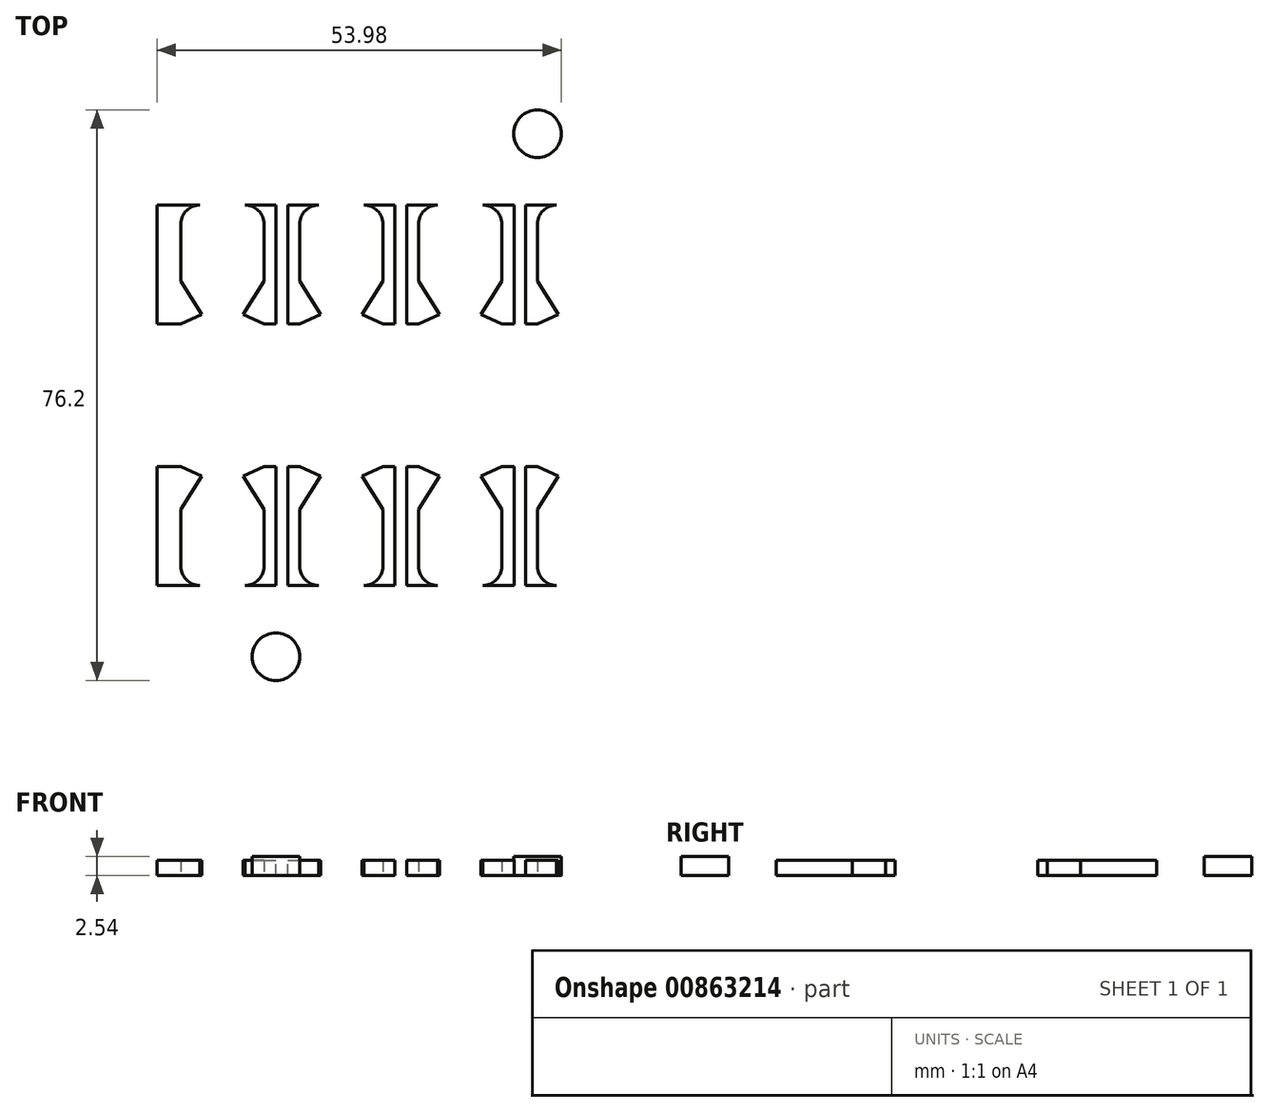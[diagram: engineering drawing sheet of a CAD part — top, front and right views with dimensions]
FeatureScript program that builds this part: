
annotation { "Feature Type Name" : "Feature", "Feature Type Description" : "" }
export const myFeature = defineFeature(function(context is Context, id is Id, definition is map)
    precondition{}
    {
        {
            var Q0;
            Q0=qCreatedBy(makeId("Top.planeOp"),FACE);
            var sketch = newSketch(context, id + "F0", { "sketchPlane" : qUnion([Q0])});
            skCircle(sketch, "E0", {"center": v(0, 0) * mm, "radius": 52.39 * mm});
            skLineSegment(sketch, "E1", {"start": v(-44.9, 26.99) * mm, "end": v(44.9, 26.99) * mm, "construction": true});
            skLineSegment(sketch, "E2", {"start": v(-44.9, -26.99) * mm, "end": v(44.9, -26.99) * mm, "construction": true});
            skLineSegment(sketch, "E3", {"start": v(-39.69, 26.99) * mm, "end": v(-39.69, -26.99) * mm, "construction": true});
            skLineSegment(sketch, "E4", {"start": v(39.69, 26.99) * mm, "end": v(39.69, -26.99) * mm, "construction": true});
            skLineSegment(sketch, "E5", {"start": v(28.57, 26.99) * mm, "end": v(28.58, -26.99) * mm, "construction": true});
            skLineSegment(sketch, "E6", {"start": v(-30.16, 26.99) * mm, "end": v(-30.16, -26.99) * mm, "construction": true});
            skLineSegment(sketch, "E7", {"start": v(-19.05, 26.99) * mm, "end": v(-19.05, -26.99) * mm, "construction": true});
            skLineSegment(sketch, "E8", {"start": v(-14.29, 26.99) * mm, "end": v(-14.29, -26.99) * mm, "construction": true});
            skLineSegment(sketch, "E9", {"start": v(-3.18, 26.99) * mm, "end": v(-3.17, -26.99) * mm, "construction": true});
            skLineSegment(sketch, "E10", {"start": v(1.59, 26.99) * mm, "end": v(1.59, -26.99) * mm, "construction": true});
            skLineSegment(sketch, "E11", {"start": v(12.7, 26.99) * mm, "end": v(12.7, -26.99) * mm, "construction": true});
            skLineSegment(sketch, "E12", {"start": v(17.46, 26.99) * mm, "end": v(17.46, -26.99) * mm, "construction": true});
            skLineSegment(sketch, "E13", {"start": v(-39.69, 25.4) * mm, "end": v(39.69, 25.4) * mm, "construction": true});
            skLineSegment(sketch, "E14", {"start": v(-39.69, -25.4) * mm, "end": v(39.69, -25.4) * mm, "construction": true});
            skLineSegment(sketch, "E15", {"start": v(-30.16, 9.53) * mm, "end": v(-27.37, 10.8) * mm});
            skLineSegment(sketch, "E16", {"start": v(-27.37, 10.8) * mm, "end": v(-30.16, 15.24) * mm});
            skLineSegment(sketch, "E17", {"start": v(-30.16, 15.24) * mm, "end": v(-30.16, 25.4) * mm});
            skLineSegment(sketch, "E18", {"start": v(-30.16, 25.4) * mm, "end": v(-33.34, 25.4) * mm});
            skLineSegment(sketch, "E19", {"start": v(-33.34, 25.4) * mm, "end": v(-33.34, 9.52) * mm});
            skLineSegment(sketch, "E20", {"start": v(-33.34, 9.52) * mm, "end": v(-30.16, 9.52) * mm});
            skLineSegment(sketch, "E21", {"start": v(-30.16, -25.4) * mm, "end": v(-30.16, -15.24) * mm});
            skLineSegment(sketch, "E22", {"start": v(-30.16, -15.24) * mm, "end": v(-27.37, -10.8) * mm});
            skLineSegment(sketch, "E23", {"start": v(-27.37, -10.8) * mm, "end": v(-30.16, -9.52) * mm});
            skLineSegment(sketch, "E24", {"start": v(-30.16, -9.53) * mm, "end": v(-33.34, -9.53) * mm});
            skLineSegment(sketch, "E25", {"start": v(-33.34, -9.53) * mm, "end": v(-33.34, -25.4) * mm});
            skLineSegment(sketch, "E26", {"start": v(-33.34, -25.4) * mm, "end": v(-30.16, -25.4) * mm});
            skLineSegment(sketch, "E27.1.0.1", {"start": v(-14.29, -9.53) * mm, "end": v(-17.46, -9.53) * mm});
            skLineSegment(sketch, "E27.1.0.2", {"start": v(-11.5, -10.8) * mm, "end": v(-14.29, -9.53) * mm});
            skLineSegment(sketch, "E27.1.0.3", {"start": v(-14.29, -15.24) * mm, "end": v(-11.5, -10.8) * mm});
            skLineSegment(sketch, "E27.1.0.4", {"start": v(-14.29, -25.4) * mm, "end": v(-14.29, -15.24) * mm});
            skLineSegment(sketch, "E27.2.0.1", {"start": v(1.59, -9.53) * mm, "end": v(-1.59, -9.53) * mm});
            skLineSegment(sketch, "E27.2.0.2", {"start": v(4.38, -10.8) * mm, "end": v(1.59, -9.53) * mm});
            skLineSegment(sketch, "E27.2.0.3", {"start": v(1.59, -15.24) * mm, "end": v(4.38, -10.8) * mm});
            skLineSegment(sketch, "E27.2.0.4", {"start": v(1.59, -25.4) * mm, "end": v(1.59, -15.24) * mm});
            skLineSegment(sketch, "E27.3.0.1", {"start": v(17.46, -9.53) * mm, "end": v(14.29, -9.53) * mm});
            skLineSegment(sketch, "E27.3.0.2", {"start": v(20.26, -10.8) * mm, "end": v(17.46, -9.53) * mm});
            skLineSegment(sketch, "E27.3.0.3", {"start": v(17.46, -15.24) * mm, "end": v(20.26, -10.8) * mm});
            skLineSegment(sketch, "E27.3.0.4", {"start": v(17.46, -25.4) * mm, "end": v(17.46, -15.24) * mm});
            skLineSegment(sketch, "E27.direction1", {"start": v(-33.34, -25.4) * mm, "end": v(-17.59, -25.4) * mm, "construction": true});
            skLineSegment(sketch, "E28", {"start": v(-34.92, 25.4) * mm, "end": v(-34.92, -25.4) * mm});
            skLineSegment(sketch, "E29", {"start": v(-34.92, -25.4) * mm, "end": v(-33.34, -25.4) * mm});
            skLineSegment(sketch, "E30", {"start": v(-30.16, -25.4) * mm, "end": v(-17.59, -25.4) * mm});
            skLineSegment(sketch, "E31", {"start": v(-14.29, -25.4) * mm, "end": v(-1.71, -25.4) * mm});
            skLineSegment(sketch, "E32", {"start": v(1.59, -25.4) * mm, "end": v(14.16, -25.4) * mm});
            skLineSegment(sketch, "E33", {"start": v(17.46, -25.4) * mm, "end": v(28.58, -25.4) * mm});
            skLineSegment(sketch, "E34", {"start": v(28.58, -25.4) * mm, "end": v(28.57, 25.4) * mm});
            skLineSegment(sketch, "E35.1.0.1", {"start": v(-17.46, 9.52) * mm, "end": v(-14.29, 9.52) * mm});
            skLineSegment(sketch, "E35.1.0.2", {"start": v(-14.29, 9.52) * mm, "end": v(-11.5, 10.8) * mm});
            skLineSegment(sketch, "E35.1.0.3", {"start": v(-11.5, 10.8) * mm, "end": v(-14.29, 15.24) * mm});
            skLineSegment(sketch, "E35.1.0.4", {"start": v(-14.29, 15.24) * mm, "end": v(-14.29, 25.4) * mm});
            skLineSegment(sketch, "E35.2.0.1", {"start": v(-1.59, 9.52) * mm, "end": v(1.59, 9.52) * mm});
            skLineSegment(sketch, "E35.2.0.2", {"start": v(1.59, 9.53) * mm, "end": v(4.38, 10.8) * mm});
            skLineSegment(sketch, "E35.2.0.3", {"start": v(4.38, 10.8) * mm, "end": v(1.59, 15.24) * mm});
            skLineSegment(sketch, "E35.2.0.4", {"start": v(1.59, 15.24) * mm, "end": v(1.59, 25.4) * mm});
            skLineSegment(sketch, "E35.3.0.1", {"start": v(14.29, 9.52) * mm, "end": v(17.46, 9.52) * mm});
            skLineSegment(sketch, "E35.3.0.2", {"start": v(17.46, 9.53) * mm, "end": v(20.26, 10.8) * mm});
            skLineSegment(sketch, "E35.3.0.3", {"start": v(20.26, 10.8) * mm, "end": v(17.46, 15.24) * mm});
            skLineSegment(sketch, "E35.3.0.4", {"start": v(17.46, 15.24) * mm, "end": v(17.46, 25.4) * mm});
            skLineSegment(sketch, "E35.direction1", {"start": v(-33.34, 9.53) * mm, "end": v(-17.46, 9.53) * mm, "construction": true});
            skLineSegment(sketch, "E36", {"start": v(28.57, 25.4) * mm, "end": v(17.46, 25.4) * mm});
            skLineSegment(sketch, "E37", {"start": v(14.29, 25.4) * mm, "end": v(1.59, 25.4) * mm});
            skLineSegment(sketch, "E38", {"start": v(-1.59, 25.4) * mm, "end": v(-14.29, 25.4) * mm});
            skLineSegment(sketch, "E39", {"start": v(-17.46, 25.4) * mm, "end": v(-30.16, 25.4) * mm});
            skLineSegment(sketch, "E40", {"start": v(-34.92, 25.4) * mm, "end": v(-33.34, 25.4) * mm});
            skLineSegment(sketch, "E41", {"start": v(-19.05, 9.52) * mm, "end": v(-14.29, 9.52) * mm});
            skLineSegment(sketch, "E42", {"start": v(-16.67, 9.52) * mm, "end": v(-16.67, 25.4) * mm, "construction": true});
            skLineSegment(sketch, "E43", {"start": v(-3.18, 9.52) * mm, "end": v(1.59, 9.52) * mm});
            skLineSegment(sketch, "E44", {"start": v(-0.8, 9.52) * mm, "end": v(-0.8, 25.4) * mm, "construction": true});
            skLineSegment(sketch, "E45", {"start": v(12.7, 9.52) * mm, "end": v(17.46, 9.52) * mm});
            skLineSegment(sketch, "E46", {"start": v(15.08, 9.52) * mm, "end": v(15.08, 25.4) * mm, "construction": true});
            skLineSegment(sketch, "E47.MirrorCS", {"start": v(-21.84, 10.8) * mm, "end": v(-19.05, 15.24) * mm});
            skLineSegment(sketch, "E48.MirrorCS", {"start": v(-19.05, 9.52) * mm, "end": v(-21.84, 10.8) * mm});
            skLineSegment(sketch, "E49.MirrorCS", {"start": v(-5.97, 10.8) * mm, "end": v(-3.17, 15.24) * mm});
            skLineSegment(sketch, "E50.MirrorCS", {"start": v(-3.17, 9.53) * mm, "end": v(-5.97, 10.8) * mm});
            skLineSegment(sketch, "E51.MirrorCS", {"start": v(9.9, 10.8) * mm, "end": v(12.7, 15.24) * mm});
            skLineSegment(sketch, "E52.MirrorCS", {"start": v(12.7, 9.53) * mm, "end": v(9.9, 10.8) * mm});
            skLineSegment(sketch, "E53", {"start": v(-14.29, -9.53) * mm, "end": v(-19.05, -9.53) * mm});
            skLineSegment(sketch, "E54", {"start": v(-16.67, -9.53) * mm, "end": v(-16.67, -25.4) * mm, "construction": true});
            skLineSegment(sketch, "E55", {"start": v(-3.17, -9.53) * mm, "end": v(1.59, -9.53) * mm});
            skLineSegment(sketch, "E56", {"start": v(-0.8, -9.53) * mm, "end": v(-0.8, -25.4) * mm, "construction": true});
            skLineSegment(sketch, "E57", {"start": v(12.7, -9.53) * mm, "end": v(17.46, -9.53) * mm});
            skLineSegment(sketch, "E58", {"start": v(15.08, -9.53) * mm, "end": v(15.08, -25.4) * mm, "construction": true});
            skLineSegment(sketch, "E59.MirrorCS", {"start": v(-19.05, 15.24) * mm, "end": v(-19.05, 25.4) * mm});
            skLineSegment(sketch, "E60.MirrorCS", {"start": v(-32.54, 9.52) * mm, "end": v(-32.54, 25.4) * mm, "construction": true});
            skLineSegment(sketch, "E61.MirrorCS", {"start": v(-3.17, 15.24) * mm, "end": v(-3.17, 25.4) * mm});
            skLineSegment(sketch, "E62.MirrorCS", {"start": v(12.7, 15.24) * mm, "end": v(12.7, 25.4) * mm});
            skLineSegment(sketch, "E63.MirrorCS", {"start": v(-19.05, -25.4) * mm, "end": v(-19.05, -15.24) * mm});
            skLineSegment(sketch, "E64.MirrorCS", {"start": v(-19.05, -15.24) * mm, "end": v(-21.84, -10.8) * mm});
            skLineSegment(sketch, "E65.MirrorCS", {"start": v(-21.84, -10.8) * mm, "end": v(-19.05, -9.53) * mm});
            skLineSegment(sketch, "E66.MirrorCS", {"start": v(-3.17, -25.4) * mm, "end": v(-3.17, -15.24) * mm});
            skLineSegment(sketch, "E67.MirrorCS", {"start": v(-3.17, -15.24) * mm, "end": v(-5.97, -10.8) * mm});
            skLineSegment(sketch, "E68.MirrorCS", {"start": v(-5.97, -10.8) * mm, "end": v(-3.17, -9.53) * mm});
            skLineSegment(sketch, "E69.MirrorCS", {"start": v(12.7, -25.4) * mm, "end": v(12.7, -15.24) * mm});
            skLineSegment(sketch, "E70.MirrorCS", {"start": v(12.7, -15.24) * mm, "end": v(9.9, -10.8) * mm});
            skLineSegment(sketch, "E71.MirrorCS", {"start": v(9.9, -10.8) * mm, "end": v(12.7, -9.53) * mm});
            skSolve(sketch);
        }
        {
            var Q0;
            Q0=makeQuery(id+"F0.imprint","IMPRINT",FACE,{"disambiguationData":[TD([[makeQuery(id+"F0.imprint","IMPRINT",EDGE,{"derivedFrom":sQuery(id+"F0.wireOp",EDGE,"E0")}),1.0]])]});
            var Q1;
            Q1=makeQuery(id+"F0.imprint","IMPRINT",FACE,{"disambiguationData":[TD([[makeQuery(id+"F0.imprint","IMPRINT",EDGE,{"derivedFrom":sQuery(id+"F0.wireOp",EDGE,"E15")}),1.0]])]});
            var Q2;
            Q2=makeQuery(id+"F0.imprint","IMPRINT",FACE,{"disambiguationData":[TD([[makeQuery(id+"F0.imprint","IMPRINT",EDGE,{"derivedFrom":sQuery(id+"F0.wireOp",EDGE,"E21")}),1.0]])]});
            extrude(context, id + "F1", {"entities" : qUnion([Q0, Q1, Q2]), "depth" : 2.54 * mm, "offsetDistance" : 25.4 * mm});
        }
        {
            var Q0;
            Q0=makeQuery(id+"F1.opExtrude","SWEPT_EDGE",EDGE,{"disambiguationData":[OSD([sQuery(id+"F0.wireOp",EDGE,"E17"),sQuery(id+"F0.wireOp",EDGE,"E18"),sQuery(id+"F0.wireOp",EDGE,"E39")])]});
            var Q1;
            Q1=makeQuery(id+"F1.opExtrude","SWEPT_EDGE",EDGE,{"disambiguationData":[OSD([sQuery(id+"F0.wireOp",EDGE,"E35.1.0.4"),sQuery(id+"F0.wireOp",EDGE,"E38")])]});
            var Q2;
            Q2=makeQuery(id+"F1.opExtrude","SWEPT_EDGE",EDGE,{"disambiguationData":[OSD([sQuery(id+"F0.wireOp",EDGE,"E35.2.0.4"),sQuery(id+"F0.wireOp",EDGE,"E37")])]});
            var Q3;
            Q3=makeQuery(id+"F1.opExtrude","SWEPT_EDGE",EDGE,{"disambiguationData":[OSD([sQuery(id+"F0.wireOp",EDGE,"E35.3.0.4"),sQuery(id+"F0.wireOp",EDGE,"E36")])]});
            var Q4;
            Q4=makeQuery(id+"F1.opExtrude","SWEPT_EDGE",EDGE,{"disambiguationData":[OSD([sQuery(id+"F0.wireOp",EDGE,"E27.3.0.4"),sQuery(id+"F0.wireOp",EDGE,"E33")])]});
            var Q5;
            Q5=makeQuery(id+"F1.opExtrude","SWEPT_EDGE",EDGE,{"disambiguationData":[OSD([sQuery(id+"F0.wireOp",EDGE,"E27.2.0.4"),sQuery(id+"F0.wireOp",EDGE,"E32")])]});
            var Q6;
            Q6=makeQuery(id+"F1.opExtrude","SWEPT_EDGE",EDGE,{"disambiguationData":[OSD([sQuery(id+"F0.wireOp",EDGE,"E27.1.0.4"),sQuery(id+"F0.wireOp",EDGE,"E31")])]});
            var Q7;
            Q7=makeQuery(id+"F1.opExtrude","SWEPT_EDGE",EDGE,{"disambiguationData":[OSD([sQuery(id+"F0.wireOp",EDGE,"E21"),sQuery(id+"F0.wireOp",EDGE,"E26"),sQuery(id+"F0.wireOp",EDGE,"E30")])]});
            var Q8;
            Q8=makeQuery(id+"F1.opExtrude","SWEPT_EDGE",EDGE,{"disambiguationData":[OSD([sQuery(id+"F0.wireOp",EDGE,"E30"),sQuery(id+"F0.wireOp",EDGE,"E63.MirrorCS")])]});
            var Q9;
            Q9=makeQuery(id+"F1.opExtrude","SWEPT_EDGE",EDGE,{"disambiguationData":[OSD([sQuery(id+"F0.wireOp",EDGE,"E31"),sQuery(id+"F0.wireOp",EDGE,"E66.MirrorCS")])]});
            var Q10;
            Q10=makeQuery(id+"F1.opExtrude","SWEPT_EDGE",EDGE,{"disambiguationData":[OSD([sQuery(id+"F0.wireOp",EDGE,"E32"),sQuery(id+"F0.wireOp",EDGE,"E69.MirrorCS")])]});
            var Q11;
            Q11=makeQuery(id+"F1.opExtrude","SWEPT_EDGE",EDGE,{"disambiguationData":[OSD([sQuery(id+"F0.wireOp",EDGE,"E37"),sQuery(id+"F0.wireOp",EDGE,"E62.MirrorCS")])]});
            var Q12;
            Q12=makeQuery(id+"F1.opExtrude","SWEPT_EDGE",EDGE,{"disambiguationData":[OSD([sQuery(id+"F0.wireOp",EDGE,"E38"),sQuery(id+"F0.wireOp",EDGE,"E61.MirrorCS")])]});
            var Q13;
            Q13=makeQuery(id+"F1.opExtrude","SWEPT_EDGE",EDGE,{"disambiguationData":[OSD([sQuery(id+"F0.wireOp",EDGE,"E39"),sQuery(id+"F0.wireOp",EDGE,"E59.MirrorCS")])]});
            fillet(context, id + "F2", {"entities" : qUnion([Q0, Q1, Q2, Q3, Q4, Q5, Q6, Q7, Q8, Q9, Q10, Q11, Q12, Q13]), "radius" : 2.54 * mm, "tangentPropagation" : true, "allowEdgeOverflow" : false});
        }
        {
            var Q0;
            Q0=makeQuery(id+"F1.opExtrude","CAP_FACE",FACE,{"disambiguationData":[OSD([sQuery(id+"F0.wireOp",EDGE,"E0"),sQuery(id+"F0.wireOp",EDGE,"E15"),sQuery(id+"F0.wireOp",EDGE,"E16"),sQuery(id+"F0.wireOp",EDGE,"E17"),sQuery(id+"F0.wireOp",EDGE,"E19"),sQuery(id+"F0.wireOp",EDGE,"E20"),sQuery(id+"F0.wireOp",EDGE,"E21"),sQuery(id+"F0.wireOp",EDGE,"E22"),sQuery(id+"F0.wireOp",EDGE,"E23"),sQuery(id+"F0.wireOp",EDGE,"E24"),sQuery(id+"F0.wireOp",EDGE,"E25"),sQuery(id+"F0.wireOp",EDGE,"E27.1.0.0"),sQuery(id+"F0.wireOp",EDGE,"E27.1.0.1"),sQuery(id+"F0.wireOp",EDGE,"E27.1.0.2"),sQuery(id+"F0.wireOp",EDGE,"E27.1.0.3"),sQuery(id+"F0.wireOp",EDGE,"E27.1.0.4"),sQuery(id+"F0.wireOp",EDGE,"E27.2.0.0"),sQuery(id+"F0.wireOp",EDGE,"E27.2.0.1"),sQuery(id+"F0.wireOp",EDGE,"E27.2.0.2"),sQuery(id+"F0.wireOp",EDGE,"E27.2.0.3"),sQuery(id+"F0.wireOp",EDGE,"E27.2.0.4"),sQuery(id+"F0.wireOp",EDGE,"E27.3.0.0"),sQuery(id+"F0.wireOp",EDGE,"E27.3.0.1"),sQuery(id+"F0.wireOp",EDGE,"E27.3.0.2"),sQuery(id+"F0.wireOp",EDGE,"E27.3.0.3"),sQuery(id+"F0.wireOp",EDGE,"E27.3.0.4"),sQuery(id+"F0.wireOp",EDGE,"E28"),sQuery(id+"F0.wireOp",EDGE,"E29"),sQuery(id+"F0.wireOp",EDGE,"E30"),sQuery(id+"F0.wireOp",EDGE,"E31"),sQuery(id+"F0.wireOp",EDGE,"E32"),sQuery(id+"F0.wireOp",EDGE,"E33"),sQuery(id+"F0.wireOp",EDGE,"E34"),sQuery(id+"F0.wireOp",EDGE,"E35.1.0.0"),sQuery(id+"F0.wireOp",EDGE,"E35.1.0.1"),sQuery(id+"F0.wireOp",EDGE,"E35.1.0.2"),sQuery(id+"F0.wireOp",EDGE,"E35.1.0.3"),sQuery(id+"F0.wireOp",EDGE,"E35.1.0.4"),sQuery(id+"F0.wireOp",EDGE,"E35.2.0.0"),sQuery(id+"F0.wireOp",EDGE,"E35.2.0.1"),sQuery(id+"F0.wireOp",EDGE,"E35.2.0.2"),sQuery(id+"F0.wireOp",EDGE,"E35.2.0.3"),sQuery(id+"F0.wireOp",EDGE,"E35.2.0.4"),sQuery(id+"F0.wireOp",EDGE,"E35.3.0.0"),sQuery(id+"F0.wireOp",EDGE,"E35.3.0.1"),sQuery(id+"F0.wireOp",EDGE,"E35.3.0.2"),sQuery(id+"F0.wireOp",EDGE,"E35.3.0.3"),sQuery(id+"F0.wireOp",EDGE,"E35.3.0.4"),sQuery(id+"F0.wireOp",EDGE,"E36"),sQuery(id+"F0.wireOp",EDGE,"E37"),sQuery(id+"F0.wireOp",EDGE,"E38"),sQuery(id+"F0.wireOp",EDGE,"E39"),sQuery(id+"F0.wireOp",EDGE,"E40")])],"isStart":false});
            var sketch = newSketch(context, id + "F3", { "sketchPlane" : qUnion([Q0])});
            skLineSegment(sketch, "E72.bottom", {"start": v(-34.92, 25.4) * mm, "end": v(28.58, 25.4) * mm});
            skLineSegment(sketch, "E72.top", {"start": v(-34.92, -25.4) * mm, "end": v(28.58, -25.4) * mm});
            skLineSegment(sketch, "E72.left", {"start": v(-34.92, 25.4) * mm, "end": v(-34.92, -25.4) * mm});
            skLineSegment(sketch, "E72.right", {"start": v(28.58, 25.4) * mm, "end": v(28.58, -25.4) * mm});
            skSolve(sketch);
        }
        {
            var Q0;
            Q0 = qSketchRegion(id + "F3", true);
            extrude(context, id + "F4", {"entities" : qUnion([Q0]), "operationType" : NewBodyOperationType.REMOVE, "oppositeDirection" : true, "depth" : 0.5 * mm, "offsetDistance" : 25.4 * mm});
        }
        {
            var Q0;
            Q0=makeQuery(id+"F1.opExtrude","CAP_FACE",FACE,{"disambiguationData":[OSD([sQuery(id+"F0.wireOp",EDGE,"E0"),sQuery(id+"F0.wireOp",EDGE,"E15"),sQuery(id+"F0.wireOp",EDGE,"E16"),sQuery(id+"F0.wireOp",EDGE,"E17"),sQuery(id+"F0.wireOp",EDGE,"E19"),sQuery(id+"F0.wireOp",EDGE,"E20"),sQuery(id+"F0.wireOp",EDGE,"E21"),sQuery(id+"F0.wireOp",EDGE,"E22"),sQuery(id+"F0.wireOp",EDGE,"E23"),sQuery(id+"F0.wireOp",EDGE,"E24"),sQuery(id+"F0.wireOp",EDGE,"E25"),sQuery(id+"F0.wireOp",EDGE,"E27.1.0.0"),sQuery(id+"F0.wireOp",EDGE,"E27.1.0.1"),sQuery(id+"F0.wireOp",EDGE,"E27.1.0.2"),sQuery(id+"F0.wireOp",EDGE,"E27.1.0.3"),sQuery(id+"F0.wireOp",EDGE,"E27.1.0.4"),sQuery(id+"F0.wireOp",EDGE,"E27.2.0.0"),sQuery(id+"F0.wireOp",EDGE,"E27.2.0.1"),sQuery(id+"F0.wireOp",EDGE,"E27.2.0.2"),sQuery(id+"F0.wireOp",EDGE,"E27.2.0.3"),sQuery(id+"F0.wireOp",EDGE,"E27.2.0.4"),sQuery(id+"F0.wireOp",EDGE,"E27.3.0.0"),sQuery(id+"F0.wireOp",EDGE,"E27.3.0.1"),sQuery(id+"F0.wireOp",EDGE,"E27.3.0.2"),sQuery(id+"F0.wireOp",EDGE,"E27.3.0.3"),sQuery(id+"F0.wireOp",EDGE,"E27.3.0.4"),sQuery(id+"F0.wireOp",EDGE,"E28"),sQuery(id+"F0.wireOp",EDGE,"E29"),sQuery(id+"F0.wireOp",EDGE,"E30"),sQuery(id+"F0.wireOp",EDGE,"E31"),sQuery(id+"F0.wireOp",EDGE,"E32"),sQuery(id+"F0.wireOp",EDGE,"E33"),sQuery(id+"F0.wireOp",EDGE,"E34"),sQuery(id+"F0.wireOp",EDGE,"E35.1.0.0"),sQuery(id+"F0.wireOp",EDGE,"E35.1.0.1"),sQuery(id+"F0.wireOp",EDGE,"E35.1.0.2"),sQuery(id+"F0.wireOp",EDGE,"E35.1.0.3"),sQuery(id+"F0.wireOp",EDGE,"E35.1.0.4"),sQuery(id+"F0.wireOp",EDGE,"E35.2.0.0"),sQuery(id+"F0.wireOp",EDGE,"E35.2.0.1"),sQuery(id+"F0.wireOp",EDGE,"E35.2.0.2"),sQuery(id+"F0.wireOp",EDGE,"E35.2.0.3"),sQuery(id+"F0.wireOp",EDGE,"E35.2.0.4"),sQuery(id+"F0.wireOp",EDGE,"E35.3.0.0"),sQuery(id+"F0.wireOp",EDGE,"E35.3.0.1"),sQuery(id+"F0.wireOp",EDGE,"E35.3.0.2"),sQuery(id+"F0.wireOp",EDGE,"E35.3.0.3"),sQuery(id+"F0.wireOp",EDGE,"E35.3.0.4"),sQuery(id+"F0.wireOp",EDGE,"E36"),sQuery(id+"F0.wireOp",EDGE,"E37"),sQuery(id+"F0.wireOp",EDGE,"E38"),sQuery(id+"F0.wireOp",EDGE,"E39"),sQuery(id+"F0.wireOp",EDGE,"E40")])],"isStart":false});
            var sketch = newSketch(context, id + "F5", { "sketchPlane" : qUnion([Q0])});
            skCircle(sketch, "E73", {"center": v(0, 0) * mm, "radius": 47 * mm});
            skCircle(sketch, "E74", {"center": v(0, 0) * mm, "radius": 52.39 * mm});
            skLineSegment(sketch, "E75", {"start": v(-41.4, 22.22) * mm, "end": v(41.4, 22.23) * mm, "construction": true});
            skLineSegment(sketch, "E76", {"start": v(-41.4, -22.23) * mm, "end": v(41.4, -22.22) * mm, "construction": true});
            skLineSegment(sketch, "E77", {"start": v(38.9, 22.23) * mm, "end": v(38.9, -22.22) * mm, "construction": true});
            skLineSegment(sketch, "E78", {"start": v(-38.9, 22.22) * mm, "end": v(-38.9, -22.23) * mm, "construction": true});
            skCircle(sketch, "E79.1.0", {"center": v(-38.5, 22.23) * mm, "radius": 2.38 * mm});
            skCircle(sketch, "E79.2.0", {"center": v(-38.5, -22.22) * mm, "radius": 2.38 * mm});
            skCircle(sketch, "E79.4.0", {"center": v(38.5, -22.23) * mm, "radius": 2.38 * mm});
            skCircle(sketch, "E79.5.0", {"center": v(38.5, 22.23) * mm, "radius": 2.38 * mm});
            skCircle(sketch, "E80", {"center": v(17.46, -34.93) * mm, "radius": 3.18 * mm});
            skCircle(sketch, "E81.MirrorC", {"center": v(17.46, 34.93) * mm, "radius": 3.18 * mm});
            skCircle(sketch, "E82.MirrorC", {"center": v(-17.46, 34.93) * mm, "radius": 3.18 * mm});
            skCircle(sketch, "E83.MirrorC", {"center": v(-17.46, -34.93) * mm, "radius": 3.18 * mm});
            skSolve(sketch);
        }
        {
            var Q0;
            Q0=makeQuery(id+"F5.imprint","IMPRINT",FACE,{"disambiguationData":[TD([[makeQuery(id+"F5.imprint","IMPRINT",EDGE,{"derivedFrom":sQuery(id+"F5.wireOp",EDGE,"E74")}),1.0]])]});
            var Q1;
            {var subQ0=sQuery(id+"F5.wireOp",EDGE,"E79.1.0");var subQ1=sQuery(id+"F5.wireOp",EDGE,"E73");var subQ2=makeQuery(id+"F5.imprint","INTERSECT",VERTEX,{"disambiguationData":[OD(0.0)],"derivedFrom":[subQ1,subQ0]});Q1=makeQuery(id+"F5.imprint","IMPRINT",FACE,{"disambiguationData":[TD([[makeQuery(id+"F5.imprint","IMPRINT",EDGE,{"disambiguationData":[TD([[subQ2,-1.0]])],"derivedFrom":subQ1}),-1.0]])]});}
            var Q2;
            {var subQ0=sQuery(id+"F5.wireOp",EDGE,"E79.2.0");var subQ1=sQuery(id+"F5.wireOp",EDGE,"E73");var subQ2=makeQuery(id+"F5.imprint","INTERSECT",VERTEX,{"disambiguationData":[OD(0.0)],"derivedFrom":[subQ1,subQ0]});Q2=makeQuery(id+"F5.imprint","IMPRINT",FACE,{"disambiguationData":[TD([[makeQuery(id+"F5.imprint","IMPRINT",EDGE,{"disambiguationData":[TD([[subQ2,-1.0]])],"derivedFrom":subQ1}),-1.0]])]});}
            var Q3;
            {var subQ0=sQuery(id+"F5.wireOp",EDGE,"E79.5.0");var subQ1=sQuery(id+"F5.wireOp",EDGE,"E73");var subQ2=makeQuery(id+"F5.imprint","INTERSECT",VERTEX,{"disambiguationData":[OD(0.0)],"derivedFrom":[subQ1,subQ0]});Q3=makeQuery(id+"F5.imprint","IMPRINT",FACE,{"disambiguationData":[TD([[makeQuery(id+"F5.imprint","IMPRINT",EDGE,{"disambiguationData":[TD([[subQ2,1.0]])],"derivedFrom":subQ1}),-1.0]])]});}
            var Q4;
            {var subQ0=sQuery(id+"F5.wireOp",EDGE,"E79.4.0");var subQ1=sQuery(id+"F5.wireOp",EDGE,"E73");var subQ2=makeQuery(id+"F5.imprint","INTERSECT",VERTEX,{"disambiguationData":[OD(0.0)],"derivedFrom":[subQ1,subQ0]});Q4=makeQuery(id+"F5.imprint","IMPRINT",FACE,{"disambiguationData":[TD([[makeQuery(id+"F5.imprint","IMPRINT",EDGE,{"disambiguationData":[TD([[subQ2,-1.0]])],"derivedFrom":subQ1}),-1.0]])]});}
            var Q5;
            Q5=makeQuery(id+"F5.imprint","IMPRINT",FACE,{"disambiguationData":[TD([[makeQuery(id+"F5.imprint","IMPRINT",EDGE,{"derivedFrom":sQuery(id+"F5.wireOp",EDGE,"E79.5.0")}),1.0]])]});
            var Q6;
            {var subQ0=sQuery(id+"F5.wireOp",EDGE,"E79.1.0");var subQ1=makeQuery(id+"F1.opExtrude","CAP_EDGE",EDGE,{"disambiguationData":[OSD([sQuery(id+"F0.wireOp",EDGE,"E28")])],"isStart":false});var subQ2=makeQuery(id+"F5.imprint","INTERSECT",VERTEX,{"disambiguationData":[OD(0.0)],"derivedFrom":[subQ1,subQ0]});Q6=makeQuery(id+"F5.imprint","IMPRINT",FACE,{"disambiguationData":[TD([[makeQuery(id+"F5.imprint","IMPRINT",EDGE,{"disambiguationData":[TD([[subQ2,-1.0]])],"derivedFrom":subQ0}),1.0]])]});}
            var Q7;
            {var subQ0=sQuery(id+"F5.wireOp",EDGE,"E79.2.0");var subQ1=makeQuery(id+"F1.opExtrude","CAP_EDGE",EDGE,{"disambiguationData":[OSD([sQuery(id+"F0.wireOp",EDGE,"E28")])],"isStart":false});var subQ2=makeQuery(id+"F5.imprint","INTERSECT",VERTEX,{"disambiguationData":[OD(0.0)],"derivedFrom":[subQ1,subQ0]});Q7=makeQuery(id+"F5.imprint","IMPRINT",FACE,{"disambiguationData":[TD([[makeQuery(id+"F5.imprint","IMPRINT",EDGE,{"disambiguationData":[TD([[subQ2,1.0]])],"derivedFrom":subQ0}),1.0]])]});}
            var Q8;
            Q8=makeQuery(id+"F5.imprint","IMPRINT",FACE,{"disambiguationData":[TD([[makeQuery(id+"F5.imprint","IMPRINT",EDGE,{"derivedFrom":sQuery(id+"F5.wireOp",EDGE,"E79.4.0")}),1.0]])]});
            var Q9;
            Q9=makeQuery(id+"F5.imprint","IMPRINT",FACE,{"disambiguationData":[TD([[makeQuery(id+"F5.imprint","IMPRINT",EDGE,{"derivedFrom":sQuery(id+"F5.wireOp",EDGE,"E80")}),1.0]])]});
            var Q10;
            Q10=makeQuery(id+"F5.imprint","IMPRINT",FACE,{"disambiguationData":[TD([[makeQuery(id+"F5.imprint","IMPRINT",EDGE,{"derivedFrom":sQuery(id+"F5.wireOp",EDGE,"E81.MirrorC")}),-1.0]])]});
            var Q11;
            Q11=makeQuery(id+"F5.imprint","IMPRINT",FACE,{"disambiguationData":[TD([[makeQuery(id+"F5.imprint","IMPRINT",EDGE,{"derivedFrom":sQuery(id+"F5.wireOp",EDGE,"E82.MirrorC")}),1.0]])]});
            var Q12;
            Q12=makeQuery(id+"F5.imprint","IMPRINT",FACE,{"disambiguationData":[TD([[makeQuery(id+"F5.imprint","IMPRINT",EDGE,{"derivedFrom":sQuery(id+"F5.wireOp",EDGE,"E83.MirrorC")}),-1.0]])]});
            extrude(context, id + "F6", {"entities" : qUnion([Q0, Q1, Q2, Q3, Q4, Q5, Q6, Q7, Q8, Q9, Q10, Q11, Q12]), "operationType" : NewBodyOperationType.REMOVE, "oppositeDirection" : true, "depth" : 25.4 * mm, "offsetDistance" : 25.4 * mm});
        }
        {
            var Q0;
            Q0=makeQuery(id+"F1.opExtrude","CAP_FACE",FACE,{"disambiguationData":[OSD([sQuery(id+"F0.wireOp",EDGE,"E0"),sQuery(id+"F0.wireOp",EDGE,"E15"),sQuery(id+"F0.wireOp",EDGE,"E16"),sQuery(id+"F0.wireOp",EDGE,"E17"),sQuery(id+"F0.wireOp",EDGE,"E19"),sQuery(id+"F0.wireOp",EDGE,"E20"),sQuery(id+"F0.wireOp",EDGE,"E21"),sQuery(id+"F0.wireOp",EDGE,"E22"),sQuery(id+"F0.wireOp",EDGE,"E23"),sQuery(id+"F0.wireOp",EDGE,"E24"),sQuery(id+"F0.wireOp",EDGE,"E25"),sQuery(id+"F0.wireOp",EDGE,"E27.1.0.2"),sQuery(id+"F0.wireOp",EDGE,"E27.1.0.3"),sQuery(id+"F0.wireOp",EDGE,"E27.1.0.4"),sQuery(id+"F0.wireOp",EDGE,"E27.2.0.2"),sQuery(id+"F0.wireOp",EDGE,"E27.2.0.3"),sQuery(id+"F0.wireOp",EDGE,"E27.2.0.4"),sQuery(id+"F0.wireOp",EDGE,"E27.3.0.2"),sQuery(id+"F0.wireOp",EDGE,"E27.3.0.3"),sQuery(id+"F0.wireOp",EDGE,"E27.3.0.4"),sQuery(id+"F0.wireOp",EDGE,"E28"),sQuery(id+"F0.wireOp",EDGE,"E29"),sQuery(id+"F0.wireOp",EDGE,"E30"),sQuery(id+"F0.wireOp",EDGE,"E31"),sQuery(id+"F0.wireOp",EDGE,"E32"),sQuery(id+"F0.wireOp",EDGE,"E33"),sQuery(id+"F0.wireOp",EDGE,"E34"),sQuery(id+"F0.wireOp",EDGE,"E35.1.0.2"),sQuery(id+"F0.wireOp",EDGE,"E35.1.0.3"),sQuery(id+"F0.wireOp",EDGE,"E35.1.0.4"),sQuery(id+"F0.wireOp",EDGE,"E35.2.0.2"),sQuery(id+"F0.wireOp",EDGE,"E35.2.0.3"),sQuery(id+"F0.wireOp",EDGE,"E35.2.0.4"),sQuery(id+"F0.wireOp",EDGE,"E35.3.0.2"),sQuery(id+"F0.wireOp",EDGE,"E35.3.0.3"),sQuery(id+"F0.wireOp",EDGE,"E35.3.0.4"),sQuery(id+"F0.wireOp",EDGE,"E36"),sQuery(id+"F0.wireOp",EDGE,"E37"),sQuery(id+"F0.wireOp",EDGE,"E38"),sQuery(id+"F0.wireOp",EDGE,"E39"),sQuery(id+"F0.wireOp",EDGE,"E40"),sQuery(id+"F0.wireOp",EDGE,"E41"),sQuery(id+"F0.wireOp",EDGE,"E43"),sQuery(id+"F0.wireOp",EDGE,"E45"),sQuery(id+"F0.wireOp",EDGE,"E47.MirrorCS"),sQuery(id+"F0.wireOp",EDGE,"E48.MirrorCS"),sQuery(id+"F0.wireOp",EDGE,"E49.MirrorCS"),sQuery(id+"F0.wireOp",EDGE,"E50.MirrorCS"),sQuery(id+"F0.wireOp",EDGE,"E51.MirrorCS"),sQuery(id+"F0.wireOp",EDGE,"E52.MirrorCS"),sQuery(id+"F0.wireOp",EDGE,"E53"),sQuery(id+"F0.wireOp",EDGE,"E55"),sQuery(id+"F0.wireOp",EDGE,"E57"),sQuery(id+"F0.wireOp",EDGE,"E59.MirrorCS"),sQuery(id+"F0.wireOp",EDGE,"E61.MirrorCS"),sQuery(id+"F0.wireOp",EDGE,"E62.MirrorCS"),sQuery(id+"F0.wireOp",EDGE,"E63.MirrorCS"),sQuery(id+"F0.wireOp",EDGE,"E64.MirrorCS"),sQuery(id+"F0.wireOp",EDGE,"E65.MirrorCS"),sQuery(id+"F0.wireOp",EDGE,"E66.MirrorCS"),sQuery(id+"F0.wireOp",EDGE,"E67.MirrorCS"),sQuery(id+"F0.wireOp",EDGE,"E68.MirrorCS"),sQuery(id+"F0.wireOp",EDGE,"E69.MirrorCS"),sQuery(id+"F0.wireOp",EDGE,"E70.MirrorCS"),sQuery(id+"F0.wireOp",EDGE,"E71.MirrorCS")])],"isStart":false});
            var sketch = newSketch(context, id + "F7", { "sketchPlane" : qUnion([Q0])});
            skLineSegment(sketch, "E84.bottom", {"start": v(-15.9, 25.4) * mm, "end": v(-17.43, 25.4) * mm});
            skLineSegment(sketch, "E84.top", {"start": v(-15.9, 9.52) * mm, "end": v(-17.43, 9.52) * mm});
            skLineSegment(sketch, "E84.left", {"start": v(-15.9, 25.4) * mm, "end": v(-15.9, 9.52) * mm});
            skLineSegment(sketch, "E84.right", {"start": v(-17.43, 25.4) * mm, "end": v(-17.43, 9.52) * mm});
            skPoint(sketch, "E84.middle", {"position": v(-16.67, 17.46) * mm});
            skLineSegment(sketch, "E85.1.0.0", {"start": v(-1.56, 25.4) * mm, "end": v(-1.56, 9.52) * mm});
            skLineSegment(sketch, "E85.1.0.1", {"start": v(-0.03, 25.4) * mm, "end": v(-0.03, 9.52) * mm});
            skLineSegment(sketch, "E85.1.0.2", {"start": v(-0.03, 9.52) * mm, "end": v(-1.56, 9.52) * mm});
            skLineSegment(sketch, "E85.1.0.3", {"start": v(-0.03, 25.4) * mm, "end": v(-1.56, 25.4) * mm});
            skLineSegment(sketch, "E85.2.0.0", {"start": v(14.32, 25.4) * mm, "end": v(14.32, 9.52) * mm});
            skLineSegment(sketch, "E85.2.0.1", {"start": v(15.84, 25.4) * mm, "end": v(15.84, 9.52) * mm});
            skLineSegment(sketch, "E85.2.0.2", {"start": v(15.84, 9.52) * mm, "end": v(14.32, 9.52) * mm});
            skLineSegment(sketch, "E85.2.0.3", {"start": v(15.84, 25.4) * mm, "end": v(14.32, 25.4) * mm});
            skLineSegment(sketch, "E85.direction1", {"start": v(-17.43, 9.52) * mm, "end": v(-1.56, 9.52) * mm, "construction": true});
            skLineSegment(sketch, "E86.MirrorCS", {"start": v(-17.43, -25.4) * mm, "end": v(-17.43, -9.52) * mm});
            skLineSegment(sketch, "E87.MirrorCS", {"start": v(-15.9, -25.4) * mm, "end": v(-15.9, -9.52) * mm});
            skLineSegment(sketch, "E88.MirrorCS", {"start": v(-15.9, -25.4) * mm, "end": v(-17.43, -25.4) * mm});
            skLineSegment(sketch, "E89.MirrorCS", {"start": v(-15.9, -9.52) * mm, "end": v(-17.43, -9.52) * mm});
            skLineSegment(sketch, "E90.MirrorCS", {"start": v(-1.56, -25.4) * mm, "end": v(-1.56, -9.52) * mm});
            skLineSegment(sketch, "E91.MirrorCS", {"start": v(-0.03, -9.52) * mm, "end": v(-1.56, -9.52) * mm});
            skLineSegment(sketch, "E92.MirrorCS", {"start": v(-0.03, -25.4) * mm, "end": v(-0.03, -9.52) * mm});
            skLineSegment(sketch, "E93.MirrorCS", {"start": v(-0.03, -25.4) * mm, "end": v(-1.56, -25.4) * mm});
            skLineSegment(sketch, "E94.MirrorCS", {"start": v(15.84, -25.4) * mm, "end": v(14.32, -25.4) * mm});
            skLineSegment(sketch, "E95.MirrorCS", {"start": v(14.32, -25.4) * mm, "end": v(14.32, -9.52) * mm});
            skLineSegment(sketch, "E96.MirrorCS", {"start": v(15.84, -9.52) * mm, "end": v(14.32, -9.52) * mm});
            skLineSegment(sketch, "E97.MirrorCS", {"start": v(15.84, -25.4) * mm, "end": v(15.84, -9.52) * mm});
            skSolve(sketch);
        }
        {
            var Q0;
            Q0 = qSketchRegion(id + "F7", true);
            extrude(context, id + "F8", {"entities" : qUnion([Q0]), "operationType" : NewBodyOperationType.REMOVE, "oppositeDirection" : true, "depth" : 25.4 * mm, "offsetDistance" : 25.4 * mm});
        }
    });
